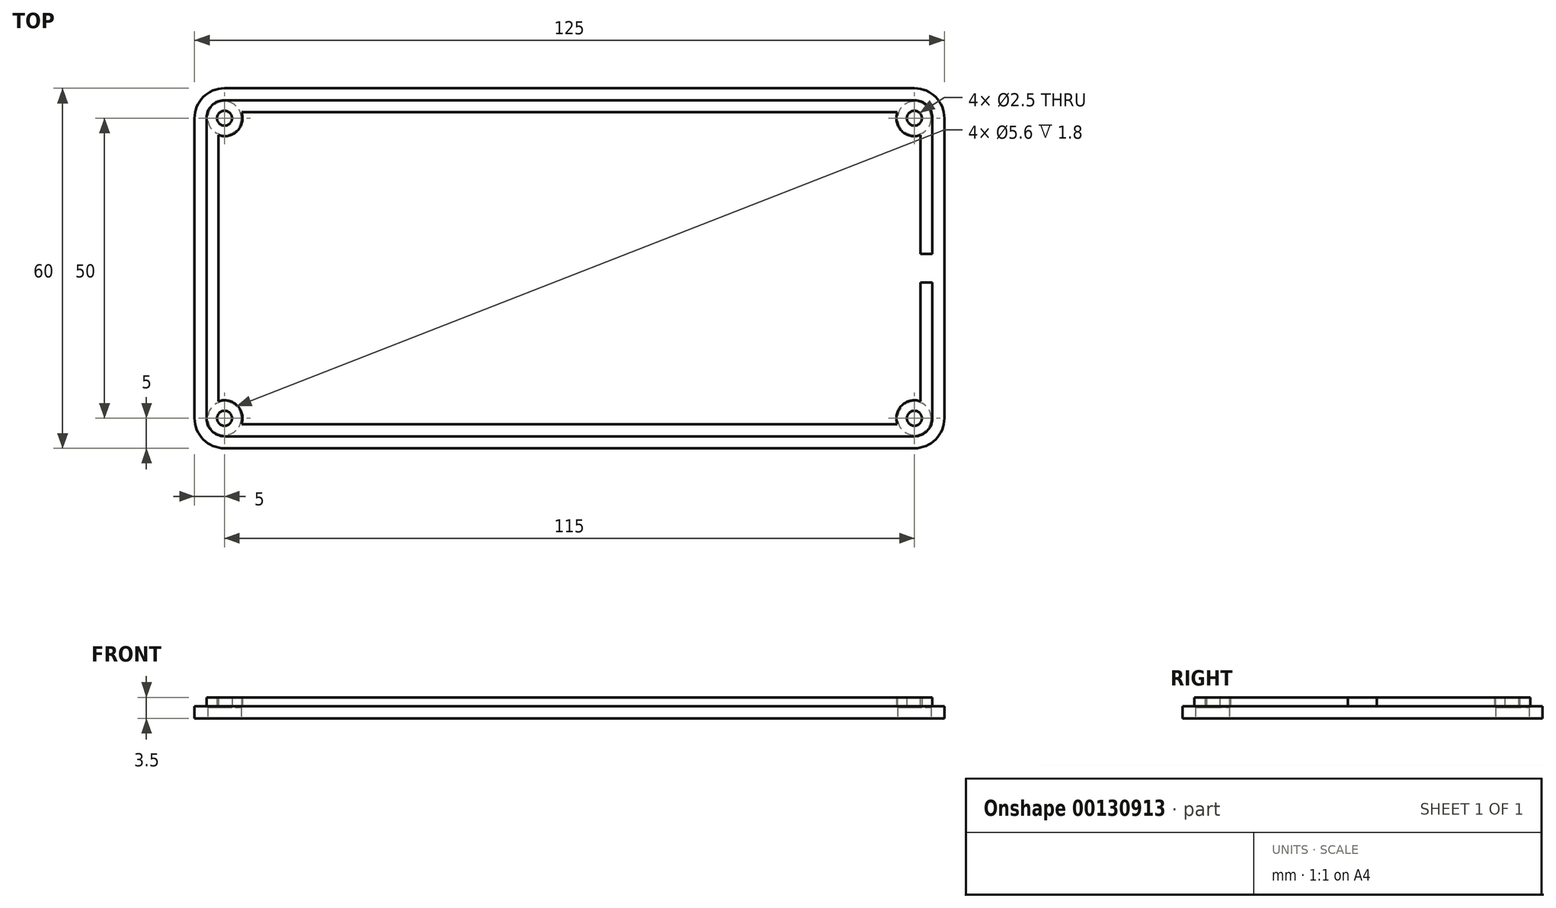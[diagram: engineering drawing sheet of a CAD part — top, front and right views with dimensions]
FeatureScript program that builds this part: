
annotation { "Feature Type Name" : "Feature", "Feature Type Description" : "" }
export const myFeature = defineFeature(function(context is Context, id is Id, definition is map)
    precondition{}
    {
        {
            var Q0;
            Q0=qCreatedBy(makeId("Top.planeOp"),FACE);
            var sketch = newSketch(context, id + "F0", { "sketchPlane" : qUnion([Q0])});
            skLineSegment(sketch, "E0.bottom", {"start": v(62.5, -30) * mm, "end": v(-62.5, -30) * mm});
            skLineSegment(sketch, "E0.top", {"start": v(62.5, 30) * mm, "end": v(-62.5, 30) * mm});
            skLineSegment(sketch, "E0.left", {"start": v(62.5, -30) * mm, "end": v(62.5, 30) * mm});
            skLineSegment(sketch, "E0.right", {"start": v(-62.5, -30) * mm, "end": v(-62.5, 30) * mm});
            skPoint(sketch, "E0.middle", {"position": v(0, 0) * mm});
            skSolve(sketch);
        }
        {
            var Q0;
            Q0=qSketchRegion(id+"F0",true);
            extrude(context, id + "F1", {"entities" : qUnion([Q0]), "depth" : 2 * mm});
        }
        {
            var Q0;
            Q0=makeQuery(id+"F1.opExtrude","CAP_FACE",FACE,{"disambiguationData":[OSD([sQuery(id+"F0.wireOp",EDGE,"E0.bottom"),sQuery(id+"F0.wireOp",EDGE,"E0.top"),sQuery(id+"F0.wireOp",EDGE,"E0.left"),sQuery(id+"F0.wireOp",EDGE,"E0.right")])],"isStart":false});
            shell(context, id + "F2", {"entities" : qUnion([Q0]), "thickness" : 2 * mm});
        }
        {
            var Q0;
            Q0=makeQuery(id+"F1.opExtrude","SWEPT_EDGE",EDGE,{"disambiguationData":[OSD([sQuery(id+"F0.wireOp",EDGE,"E0.bottom"),sQuery(id+"F0.wireOp",EDGE,"E0.left")])]});
            var Q1;
            Q1=makeQuery(id+"F1.opExtrude","SWEPT_EDGE",EDGE,{"disambiguationData":[OSD([sQuery(id+"F0.wireOp",EDGE,"E0.top"),sQuery(id+"F0.wireOp",EDGE,"E0.left")])]});
            var Q2;
            Q2=makeQuery(id+"F1.opExtrude","SWEPT_EDGE",EDGE,{"disambiguationData":[OSD([sQuery(id+"F0.wireOp",EDGE,"E0.top"),sQuery(id+"F0.wireOp",EDGE,"E0.right")])]});
            var Q3;
            Q3=makeQuery(id+"F1.opExtrude","SWEPT_EDGE",EDGE,{"disambiguationData":[OSD([sQuery(id+"F0.wireOp",EDGE,"E0.bottom"),sQuery(id+"F0.wireOp",EDGE,"E0.right")])]});
            fillet(context, id + "F3", {"entities" : qUnion([Q0, Q1, Q2, Q3]), "radius" : 5 * mm, "tangentPropagation" : true, "allowEdgeOverflow" : false});
        }
        {
            var Q0;
            Q0=makeQuery(id+"FOXE2twzRzq7qzZ_1.boolean.opBoolean","MERGE",FACE,{"derivedFrom":[makeQuery(id+"F1.opExtrude","CAP_FACE",FACE,{"disambiguationData":[OSD([sQuery(id+"F0.wireOp",EDGE,"E0.bottom"),sQuery(id+"F0.wireOp",EDGE,"E0.top"),sQuery(id+"F0.wireOp",EDGE,"E0.left"),sQuery(id+"F0.wireOp",EDGE,"E0.right")])],"isStart":false}),makeQuery(id+"FOXE2twzRzq7qzZ_1.opExtrude","CAP_FACE",FACE,{"disambiguationData":[OSD([sQuery(id+"FJAjS0KHCnbzQbk_1.wireOp",EDGE,"Br0cbSxU-Jofu-FCIU-9iMb-ijO8t87v1jQX.bottom"),sQuery(id+"FJAjS0KHCnbzQbk_1.wireOp",EDGE,"Br0cbSxU-Jofu-FCIU-9iMb-ijO8t87v1jQX.top"),sQuery(id+"FJAjS0KHCnbzQbk_1.wireOp",EDGE,"Br0cbSxU-Jofu-FCIU-9iMb-ijO8t87v1jQX.left"),sQuery(id+"FJAjS0KHCnbzQbk_1.wireOp",EDGE,"Br0cbSxU-Jofu-FCIU-9iMb-ijO8t87v1jQX.right")])],"isStart":false}),makeQuery(id+"FOXE2twzRzq7qzZ_1.opExtrude","CAP_FACE",FACE,{"disambiguationData":[OSD([sQuery(id+"FJAjS0KHCnbzQbk_1.wireOp",EDGE,"3fd054f4-3fd5-4327-9032-f4dd330a39b90.MirrorCS"),sQuery(id+"FJAjS0KHCnbzQbk_1.wireOp",EDGE,"7669ca2f-4276-47ad-977a-a8db704cf9530.MirrorCS"),sQuery(id+"FJAjS0KHCnbzQbk_1.wireOp",EDGE,"78da999b-ac20-49cd-a0c9-9e1dea4bbdc90.MirrorCS"),sQuery(id+"FJAjS0KHCnbzQbk_1.wireOp",EDGE,"415c9d2e-70f6-4269-9fa8-7dbf6befb3350.MirrorCS")])],"isStart":false}),makeQuery(id+"FOXE2twzRzq7qzZ_1.opExtrude","CAP_FACE",FACE,{"disambiguationData":[OSD([sQuery(id+"FJAjS0KHCnbzQbk_1.wireOp",EDGE,"c8ebc39b-b2ea-4fea-8fb1-2553651146340.MirrorCS"),sQuery(id+"FJAjS0KHCnbzQbk_1.wireOp",EDGE,"b664797a-d0f2-4005-806f-4d9f75d7933a0.MirrorCS"),sQuery(id+"FJAjS0KHCnbzQbk_1.wireOp",EDGE,"672e479e-c1a9-4b87-8cd9-81af36f87a280.MirrorCS"),sQuery(id+"FJAjS0KHCnbzQbk_1.wireOp",EDGE,"eb145049-44e3-489c-9830-a6b32bf15db80.MirrorCS")])],"isStart":false}),makeQuery(id+"FOXE2twzRzq7qzZ_1.opExtrude","CAP_FACE",FACE,{"disambiguationData":[OSD([sQuery(id+"FJAjS0KHCnbzQbk_1.wireOp",EDGE,"3e3ba1d9-6bb4-4d99-bfb3-7c5bded82f260.MirrorCS"),sQuery(id+"FJAjS0KHCnbzQbk_1.wireOp",EDGE,"545c4789-970f-4a02-918a-0721b3faf0d60.MirrorCS"),sQuery(id+"FJAjS0KHCnbzQbk_1.wireOp",EDGE,"f5dbf4c7-1728-4f23-a336-ca939b137ab30.MirrorCS"),sQuery(id+"FJAjS0KHCnbzQbk_1.wireOp",EDGE,"f5c5b169-1aaa-4fb4-8cc0-5472c8d7a6b70.MirrorCS")])],"isStart":false})]});
            var sketch = newSketch(context, id + "F4", { "sketchPlane" : qUnion([Q0])});
            skCircle(sketch, "E1", {"center": v(-57.5, 25) * mm, "radius": 1.25 * mm});
            skCircle(sketch, "E2", {"center": v(-57.5, -25) * mm, "radius": 1.25 * mm});
            skCircle(sketch, "E3", {"center": v(57.5, 25) * mm, "radius": 1.25 * mm});
            skCircle(sketch, "E4", {"center": v(57.5, -25) * mm, "radius": 1.25 * mm});
            skSolve(sketch);
        }
        {
            var Q0;
            Q0=qSketchRegion(id+"F4",true);
            extrude(context, id + "F5", {"entities" : qUnion([Q0]), "operationType" : NewBodyOperationType.REMOVE, "depth" : 10 * mm, "symmetric" : true});
        }
        {
            var Q0;
            Q0=makeQuery(id+"F1.opExtrude","CAP_FACE",FACE,{"disambiguationData":[OSD([sQuery(id+"F0.wireOp",EDGE,"E0.bottom"),sQuery(id+"F0.wireOp",EDGE,"E0.top"),sQuery(id+"F0.wireOp",EDGE,"E0.left"),sQuery(id+"F0.wireOp",EDGE,"E0.right")])],"isStart":false});
            var sketch = newSketch(context, id + "F6", { "sketchPlane" : qUnion([Q0])});
            skLineSegment(sketch, "E5.0", {"start": v(57.5, 28) * mm, "end": v(-57.5, 28) * mm});
            skLineSegment(sketch, "E6.0", {"start": v(-60.5, -25) * mm, "end": v(-60.5, 25) * mm});
            skLineSegment(sketch, "E7.0", {"start": v(57.5, -28) * mm, "end": v(-57.5, -28) * mm});
            skLineSegment(sketch, "E8.0", {"start": v(60.5, -25) * mm, "end": v(60.5, 25) * mm});
            skArc(sketch, "E9.filletArc", {"start": v(60.5, 25) * mm, "mid": v(59.62, 27.12) * mm, "end": v(57.5, 28) * mm});
            skArc(sketch, "E10.filletArc", {"start": v(57.5, -28) * mm, "mid": v(59.62, -27.12) * mm, "end": v(60.5, -25) * mm});
            skArc(sketch, "E11.filletArc", {"start": v(-57.5, 28) * mm, "mid": v(-59.62, 27.12) * mm, "end": v(-60.5, 25) * mm});
            skArc(sketch, "E12.filletArc", {"start": v(-60.5, -25) * mm, "mid": v(-59.62, -27.12) * mm, "end": v(-57.5, -28) * mm});
            skLineSegment(sketch, "E13.0", {"start": v(58.5, 26) * mm, "end": v(-58.5, 26) * mm});
            skLineSegment(sketch, "E13.1", {"start": v(58.5, -26) * mm, "end": v(58.5, 26) * mm});
            skLineSegment(sketch, "E13.2", {"start": v(58.5, -26) * mm, "end": v(-58.5, -26) * mm});
            skLineSegment(sketch, "E13.3", {"start": v(-58.5, -26) * mm, "end": v(-58.5, 26) * mm});
            skSolve(sketch);
        }
        {
            var Q0;
            Q0=qSketchRegion(id+"F6",true);
            extrude(context, id + "F7", {"entities" : qUnion([Q0]), "operationType" : NewBodyOperationType.ADD, "depth" : 1.5 * mm});
        }
        {
            var Q0;
            {var subQ0=sQuery(id+"F6.wireOp",EDGE,"E13.0");var subQ1=sQuery(id+"F6.wireOp",EDGE,"E13.3");var subQ2=sQuery(id+"F6.wireOp",EDGE,"E13.2");var subQ3=sQuery(id+"F6.wireOp",EDGE,"E13.1");Q0=makeQuery(id+"F7.boolean.opBoolean","SPLIT",FACE,{"disambiguationData":[TD([makeQuery(id+"F5.boolean.opBoolean","COPY",FACE,{"derivedFrom":makeQuery(id+"F5.opExtrude","SWEPT_FACE",FACE,{"disambiguationData":[OSD([sQuery(id+"F4.wireOp",EDGE,"E1")])]})}),makeQuery(id+"F5.boolean.opBoolean","COPY",FACE,{"derivedFrom":makeQuery(id+"F5.opExtrude","SWEPT_FACE",FACE,{"disambiguationData":[OSD([sQuery(id+"F4.wireOp",EDGE,"E2")])]})}),makeQuery(id+"F5.boolean.opBoolean","COPY",FACE,{"derivedFrom":makeQuery(id+"F5.opExtrude","SWEPT_FACE",FACE,{"disambiguationData":[OSD([sQuery(id+"F4.wireOp",EDGE,"E3")])]})}),makeQuery(id+"F5.boolean.opBoolean","COPY",FACE,{"derivedFrom":makeQuery(id+"F5.opExtrude","SWEPT_FACE",FACE,{"disambiguationData":[OSD([sQuery(id+"F4.wireOp",EDGE,"E4")])]})}),makeQuery(id+"F7.opExtrude","CAP_FACE",FACE,{"disambiguationData":[OSD([sQuery(id+"F6.wireOp",EDGE,"E5.0"),sQuery(id+"F6.wireOp",EDGE,"E6.0"),sQuery(id+"F6.wireOp",EDGE,"E7.0"),sQuery(id+"F6.wireOp",EDGE,"E8.0"),sQuery(id+"F6.wireOp",EDGE,"E9.filletArc"),sQuery(id+"F6.wireOp",EDGE,"E10.filletArc"),sQuery(id+"F6.wireOp",EDGE,"E11.filletArc"),sQuery(id+"F6.wireOp",EDGE,"E12.filletArc"),subQ0,subQ3,subQ2,subQ1])],"isStart":true}),makeQuery(id+"F7.opExtrude","SWEPT_FACE",FACE,{"disambiguationData":[OSD([subQ0])]}),makeQuery(id+"F7.opExtrude","SWEPT_FACE",FACE,{"disambiguationData":[OSD([subQ3])]}),makeQuery(id+"F7.opExtrude","SWEPT_FACE",FACE,{"disambiguationData":[OSD([subQ2])]}),makeQuery(id+"F7.opExtrude","SWEPT_FACE",FACE,{"disambiguationData":[OSD([subQ1])]})])],"derivedFrom":makeQuery(id+"F1.opExtrude","CAP_FACE",FACE,{"disambiguationData":[OSD([sQuery(id+"F0.wireOp",EDGE,"E0.bottom"),sQuery(id+"F0.wireOp",EDGE,"E0.top"),sQuery(id+"F0.wireOp",EDGE,"E0.left"),sQuery(id+"F0.wireOp",EDGE,"E0.right")])],"isStart":false})});}
            var sketch = newSketch(context, id + "F8", { "sketchPlane" : qUnion([Q0])});
            skCircle(sketch, "E14", {"center": v(-57.5, 25) * mm, "radius": 3 * mm});
            skCircle(sketch, "E15", {"center": v(-57.5, -25) * mm, "radius": 3 * mm});
            skCircle(sketch, "E16", {"center": v(57.5, -25) * mm, "radius": 3 * mm});
            skCircle(sketch, "E17", {"center": v(57.5, 25) * mm, "radius": 3 * mm});
            skSolve(sketch);
        }
        {
            var Q0;
            Q0=qSketchRegion(id+"F8",true);
            extrude(context, id + "F9", {"entities" : qUnion([Q0]), "operationType" : NewBodyOperationType.ADD, "depth" : 1.5 * mm});
        }
        {
            var Q0;
            Q0=makeQuery(id+"F9.boolean.opBoolean","MERGE",FACE,{"derivedFrom":[makeQuery(id+"F7.opExtrude","CAP_FACE",FACE,{"disambiguationData":[OSD([sQuery(id+"F6.wireOp",EDGE,"E5.0"),sQuery(id+"F6.wireOp",EDGE,"E6.0"),sQuery(id+"F6.wireOp",EDGE,"E7.0"),sQuery(id+"F6.wireOp",EDGE,"E8.0"),sQuery(id+"F6.wireOp",EDGE,"E9.filletArc"),sQuery(id+"F6.wireOp",EDGE,"E10.filletArc"),sQuery(id+"F6.wireOp",EDGE,"E11.filletArc"),sQuery(id+"F6.wireOp",EDGE,"E12.filletArc"),sQuery(id+"F6.wireOp",EDGE,"E13.0"),sQuery(id+"F6.wireOp",EDGE,"E13.1"),sQuery(id+"F6.wireOp",EDGE,"E13.2"),sQuery(id+"F6.wireOp",EDGE,"E13.3")])],"isStart":false}),makeQuery(id+"F9.opExtrude","CAP_FACE",FACE,{"disambiguationData":[OSD([sQuery(id+"F8.wireOp",EDGE,"E14")])],"isStart":false}),makeQuery(id+"F9.opExtrude","CAP_FACE",FACE,{"disambiguationData":[OSD([sQuery(id+"F8.wireOp",EDGE,"E15")])],"isStart":false}),makeQuery(id+"F9.opExtrude","CAP_FACE",FACE,{"disambiguationData":[OSD([sQuery(id+"F8.wireOp",EDGE,"E16")])],"isStart":false}),makeQuery(id+"F9.opExtrude","CAP_FACE",FACE,{"disambiguationData":[OSD([sQuery(id+"F8.wireOp",EDGE,"E17")])],"isStart":false})]});
            var sketch = newSketch(context, id + "F10", { "sketchPlane" : qUnion([Q0])});
            skCircle(sketch, "E18", {"center": v(57.5, -25) * mm, "radius": 1.25 * mm});
            skCircle(sketch, "E19", {"center": v(57.5, 25) * mm, "radius": 1.25 * mm});
            skCircle(sketch, "E20", {"center": v(-57.5, 25) * mm, "radius": 1.25 * mm});
            skCircle(sketch, "E21", {"center": v(-57.5, -25) * mm, "radius": 1.25 * mm});
            skSolve(sketch);
        }
        {
            var Q0;
            Q0=qSketchRegion(id+"F10",true);
            extrude(context, id + "F11", {"entities" : qUnion([Q0]), "operationType" : NewBodyOperationType.REMOVE, "endBound" : BoundingType.UP_TO_NEXT, "oppositeDirection" : true, "depth" : 25 * mm});
        }
        {
            var Q0;
            Q0=makeQuery(id+"F1.opExtrude","CAP_FACE",FACE,{"disambiguationData":[OSD([sQuery(id+"F0.wireOp",EDGE,"E0.bottom"),sQuery(id+"F0.wireOp",EDGE,"E0.top"),sQuery(id+"F0.wireOp",EDGE,"E0.left"),sQuery(id+"F0.wireOp",EDGE,"E0.right")])],"isStart":true});
            var sketch = newSketch(context, id + "F12", { "sketchPlane" : qUnion([Q0])});
            skCircle(sketch, "E22", {"center": v(-57.5, 25) * mm, "radius": 2.8 * mm});
            skCircle(sketch, "E23", {"center": v(57.5, 25) * mm, "radius": 2.8 * mm});
            skCircle(sketch, "E24", {"center": v(-57.5, -25) * mm, "radius": 2.8 * mm});
            skCircle(sketch, "E25", {"center": v(57.5, -25) * mm, "radius": 2.8 * mm});
            skSolve(sketch);
        }
        {
            var Q0;
            Q0=qSketchRegion(id+"F12",true);
            extrude(context, id + "F13", {"entities" : qUnion([Q0]), "operationType" : NewBodyOperationType.REMOVE, "oppositeDirection" : true, "depth" : 1.8 * mm});
        }
        {
            var Q0;
            Q0=makeQuery(id+"F7.opExtrude","SWEPT_FACE",FACE,{"disambiguationData":[OSD([sQuery(id+"F6.wireOp",EDGE,"E8.0")])]});
            var sketch = newSketch(context, id + "F14", { "sketchPlane" : qUnion([Q0])});
            skLineSegment(sketch, "E26.bottom", {"start": v(2.4, 2) * mm, "end": v(-2.4, 2) * mm});
            skLineSegment(sketch, "E26.left", {"start": v(2.4, 2) * mm, "end": v(2.4, 3.5) * mm});
            skLineSegment(sketch, "E26.right", {"start": v(-2.4, 2) * mm, "end": v(-2.4, 3.5) * mm});
            skPoint(sketch, "E26.middle", {"position": v(0, 3.5) * mm});
            skLineSegment(sketch, "E27", {"start": v(-2.4, 3.5) * mm, "end": v(2.4, 3.5) * mm});
            skPoint(sketch, "E26.top.end.orphan", {"position": v(-2.4, 5) * mm});
            skPoint(sketch, "E28.orphan", {"position": v(2.4, 5) * mm});
            skSolve(sketch);
        }
        {
            var Q0;
            Q0=qSketchRegion(id+"F14",true);
            extrude(context, id + "F15", {"entities" : qUnion([Q0]), "operationType" : NewBodyOperationType.REMOVE, "endBound" : BoundingType.UP_TO_NEXT, "oppositeDirection" : true, "depth" : 25 * mm});
        }
    });
